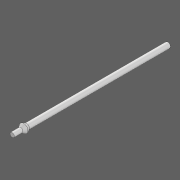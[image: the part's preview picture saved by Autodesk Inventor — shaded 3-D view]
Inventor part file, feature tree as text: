
AUTODESK INVENTOR PART (.ipt)
format: ipt  version: 2020 (Build 240168000, 168)  size: 92,160 bytes
history: native  units: in
note: dims shown in document units (in); Inventor stores cm internally (conversion verified against a paired STEP export)
features: revolve x1, sketch x1
ambient origin geometry x8: Origin, YZ Plane, XZ Plane, XY Plane, X Axis, Y Axis, Z Axis, Center Point
bodies: Solid1 (feature_tree)
feature tree (2):
  revolve  "Revolution1"  [1 undecoded]
  sketch  "Sketch1"  dims[d0=90.0deg d5=7.0866in d8=0.1969in d12=0.2362in d14=0.3937in d15=0.2756in d16=0.1969in]
note: 1 required parameter value undecoded (feature->parameter linkage not recoverable at this tier; creation-order binding heuristic only, values carry confidence <= 0.55)
